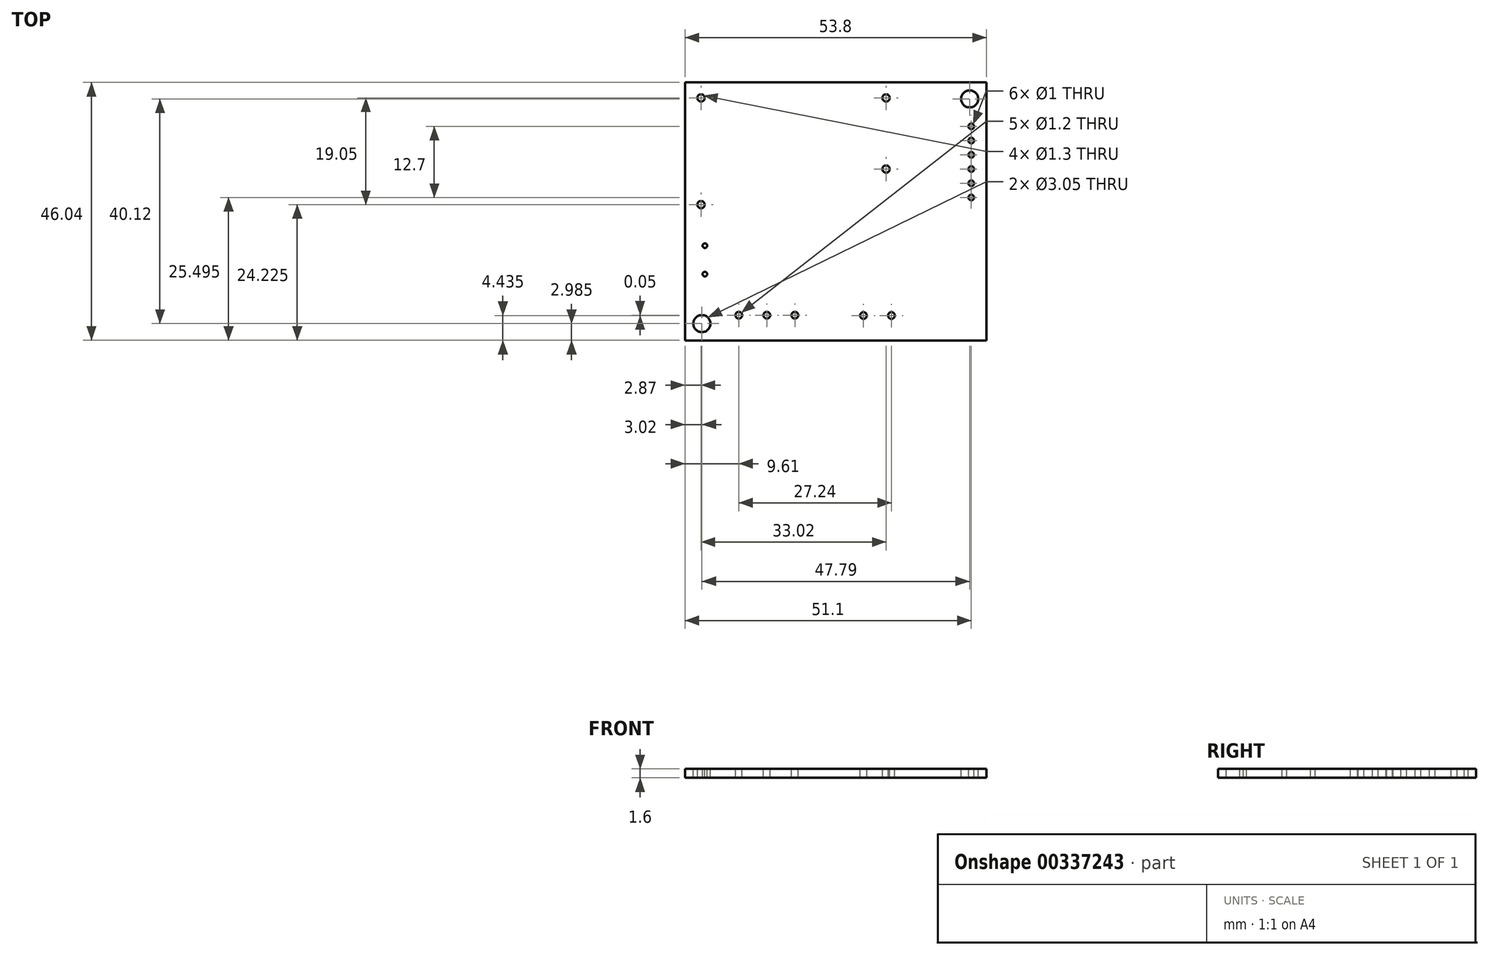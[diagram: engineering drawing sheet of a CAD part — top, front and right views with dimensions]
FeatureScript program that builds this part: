
annotation { "Feature Type Name" : "Feature", "Feature Type Description" : "" }
export const myFeature = defineFeature(function(context is Context, id is Id, definition is map)
    precondition{}
    {
        {
            var Q0;
            Q0=qCreatedBy(makeId("Top.planeOp"),FACE);
            var sketch = newSketch(context, id + "F0", { "sketchPlane" : qUnion([Q0])});
            skLineSegment(sketch, "E0.bottom", {"start": v(26.9, -23.02) * mm, "end": v(-26.9, -23.03) * mm});
            skLineSegment(sketch, "E0.top", {"start": v(26.9, 23.03) * mm, "end": v(-26.9, 23.02) * mm});
            skLineSegment(sketch, "E0.left", {"start": v(26.9, -23.02) * mm, "end": v(26.9, 23.03) * mm});
            skLineSegment(sketch, "E0.right", {"start": v(-26.9, -23.03) * mm, "end": v(-26.9, 23.02) * mm});
            skPoint(sketch, "E0.middle", {"position": v(0, 0) * mm});
            skCircle(sketch, "E1", {"center": v(-23.88, -20.04) * mm, "radius": 1.52 * mm});
            skCircle(sketch, "E2", {"center": v(23.9, 20.09) * mm, "radius": 1.52 * mm});
            skCircle(sketch, "E3", {"center": v(24.2, 15.18) * mm, "radius": 0.5 * mm});
            skCircle(sketch, "E4", {"center": v(24.2, 12.64) * mm, "radius": 0.5 * mm});
            skCircle(sketch, "E5", {"center": v(24.2, 10.1) * mm, "radius": 0.5 * mm});
            skCircle(sketch, "E6", {"center": v(24.2, 7.56) * mm, "radius": 0.5 * mm});
            skCircle(sketch, "E7", {"center": v(24.2, 5.02) * mm, "radius": 0.5 * mm});
            skCircle(sketch, "E8", {"center": v(24.2, 2.48) * mm, "radius": 0.5 * mm});
            skCircle(sketch, "E9", {"center": v(-24.03, 20.25) * mm, "radius": 0.65 * mm});
            skCircle(sketch, "E10", {"center": v(-24.03, 1.2) * mm, "radius": 0.65 * mm});
            skCircle(sketch, "E11", {"center": v(8.99, 20.26) * mm, "radius": 0.65 * mm});
            skCircle(sketch, "E12", {"center": v(8.99, 7.55) * mm, "radius": 0.65 * mm});
            skCircle(sketch, "E13", {"center": v(-23.34, -6.12) * mm, "radius": 0.4 * mm});
            skCircle(sketch, "E14", {"center": v(-23.34, -11.2) * mm, "radius": 0.4 * mm});
            skCircle(sketch, "E15", {"center": v(-17.29, -18.54) * mm, "radius": 0.6 * mm});
            skCircle(sketch, "E16", {"center": v(-12.29, -18.54) * mm, "radius": 0.6 * mm});
            skCircle(sketch, "E17", {"center": v(-7.29, -18.54) * mm, "radius": 0.6 * mm});
            skCircle(sketch, "E18", {"center": v(4.95, -18.59) * mm, "radius": 0.6 * mm});
            skCircle(sketch, "E19", {"center": v(9.95, -18.59) * mm, "radius": 0.6 * mm});
            skSolve(sketch);
        }
        {
            var Q0;
            Q0=makeQuery(id+"F0.imprint","IMPRINT",FACE,{"disambiguationData":[TD([[makeQuery(id+"F0.imprint","IMPRINT",EDGE,{"derivedFrom":sQuery(id+"F0.wireOp",EDGE,"E0.bottom")}),-1.0]])]});
            extrude(context, id + "F1", {"entities" : qUnion([Q0]), "oppositeDirection" : true, "depth" : 1.6 * mm});
        }
    });
